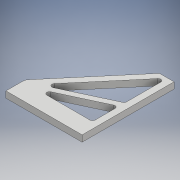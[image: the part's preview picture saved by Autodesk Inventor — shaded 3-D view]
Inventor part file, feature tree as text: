
AUTODESK INVENTOR PART (.ipt)
format: ipt  version: 2018.3 (Build 223284000, 284)  size: 141,312 bytes
history: native  units: mm
features: extrude x4, sketch x4, fillet x1
ambient origin geometry x8: Origin, YZ Plane, XZ Plane, XY Plane, X Axis, Y Axis, Z Axis, Center Point
bodies: Solid1 (feature_tree)
feature tree (9):
  extrude  "Extrusion1"  Depth=15.0mm
  extrude  "Extrusion2"  Depth=5.0mm TaperAngle=0.0deg
  fillet  "Fillet1"  Radius=5.0mm
  extrude  "Extrusion3"  Depth=5.0mm TaperAngle=0.0deg
  extrude  "Extrusion4"  Depth=5.0mm TaperAngle=0.0deg
  sketch  "Sketch1"  dims[d0=60.0mm d1=15.0mm]
  sketch  "Sketch2"  dims[d2=5.0mm d3=5.0mm d4=0.0mm d5=5.0mm d6=0.0mm]
  sketch  "Sketch3"  dims[d7=2.0mm d8=5.0mm d9=0.0mm]
  sketch  "Sketch4"  dims[d10=3.0mm d11=5.0mm d12=0.0mm]
